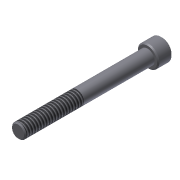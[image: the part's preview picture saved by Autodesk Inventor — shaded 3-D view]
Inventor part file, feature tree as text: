
AUTODESK INVENTOR PART (.ipt)
format: ipt  version: 2013 (Build 170138000, 138)  size: 100,352 bytes
history: native  units: in
note: dims shown in document units (in); Inventor stores cm internally (conversion verified against a paired STEP export)
features: extrude x3, sketch x3, chamfer x1, thread x1
ambient origin geometry x8: Origin, YZ Plane, XZ Plane, XY Plane, X Axis, Y Axis, Z Axis, Center Point
bodies: Solid1 (feature_tree)
feature tree (8):
  extrude  "Extrusion1"  Depth=2.25in TaperAngle=0.0deg
  extrude  "Extrusion2"  Depth=0.25in TaperAngle=0.0deg
  extrude  "Extrusion3"  Depth=0.125in TaperAngle=0.0deg
  chamfer  "Chamfer1"  Distance=0.02in Angle=45.0deg
  thread  "Thread1"  [1 undecoded]
  sketch  "Sketch1"  dims[d0=0.25in d1=2.25in d2=0.0in]
  sketch  "Sketch2"  dims[d3=0.375in d4=0.25in d5=0.0in]
  sketch  "Sketch3"  dims[d6=0.1875in d7=0.125in d8=0.0in d9=0.02in d10=0.125in d11=45.0deg d12=1.0in d13=0.0in]
note: 1 required parameter value undecoded (feature->parameter linkage not recoverable at this tier; creation-order binding heuristic only, values carry confidence <= 0.55)
